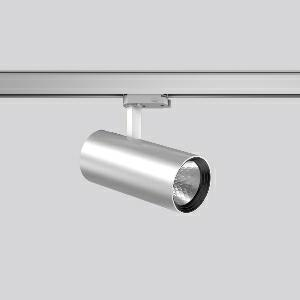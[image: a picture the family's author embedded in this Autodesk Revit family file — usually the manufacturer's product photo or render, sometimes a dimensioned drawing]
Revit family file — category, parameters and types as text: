
# Revit family: deecos_s_mini_742195_004_2_76_cb85
name_source: partatom
category: Lighting Fixtures
units: mm (PartAtom-declared; Revit-internal decimal feet)

## family parameters
Cut with Voids When Loaded = No
Host = Face
Light Source = No
Part Type = Normal
Room Calculation Point = No
Round Connector Dimension = Use Diameter
Shared = No

## types (1)
- DEECOS S mini (1 x LED Modul 927, 2400 lm, 2700)
    Apparent Load = 20 VA
    Approval mark = CE
    CIE Flux Codes = 100 100 100 100 100
    Color Rendering = 92
    Color Temperature = 2700
    Default Elevation = 1800 mm
    Description = Series: DEECOS S mini
LED surface-mounted projector in modern design with no visible cooling ribs. Housing: die-cast aluminium, powder-coated. Rotation range: 356°. Swivel range: 90°. Black plastic ring and recessed LED to prevent glare from the side. Optical assembly with reflector made of MIRO-Silver with 98% total light reflection for outstanding efficiency - can be changed without tools. Best colour rendering index Ra>90. With adapter for RZB 3-circuit DALI tracks. Suitable for Track on ceiling, Wall track. High quality converter without flickering and stroboscopic effect. The following accessories can be mounted without use of tools: interchangeable lenses, decorative glasses, honeycomb louvre, clear and frosted diffusers, white interchangeable plastic ring. 
Colour: silver
Diameter: 87 mm
Height: 214 mm
Lamp: LED
Socket: without socket
Colour temperature: 2700K
Colour rendering index (CRI): 92
System power: 20 W
Rated luminous flux: 2400 lm
Luminous efficiency: 120 lm/W
Control gear: Converter, dimmable, DALI
Protection class: I
Type of protection: IP 20
    Height = 214 mm
    Lamp = 1 x LED Modul 927
    Lamp Light Flux = 2400 lm
    Lamp count = 1
    Length = 87 mm
    Lifetime = 50000 h
    Luminous efficacy = 120 lm/W
    Manufacturer = RZB
    ModVariant = No
    Model = 742195.004.2.76
    Mounting Place = Ceiling
    Mounting Type = Rail mounted
    Number of Poles = 1
    OnlyDefault = Yes
    Power Factor = 1
    Product Name = DEECOS S mini
    Product group = Track mounted projectors
    ProductGroupID = 301
    Protection Class = Protection class I
    Protection Degree = IP 20
    RLX_Detail_Level = 1
    RLX_Emergency_Light_Flux = 0 lm
    RLX_Emergency_Type = 0
    RLX_Emergency_Type_DB = No
    RlxData = <blob elided: 37041 chars, md5=1e53af6a>
    Socket = socket
    Standby Power = 0 W
    System Light Flux = 2400 lm
    System Power = 20 W
    Type Comments = Product without accessories
    Type Image = 741926.004.jpg
    URL = http://relux.com
    VarID = ---
    Voltage = 230 V
    Voltage Range = 220-240 V
    Weight = 0.00 kg
    Width = 0 mm  [stored 0 ft]

note: [stored X ft] marks values corroborated as IEEE doubles in the binary element streams (Revit-internal decimal feet)

## geometry (parser evidence)
native form markers: Blend x4, Sweep x13
no freeform markers — native parametric forms only
